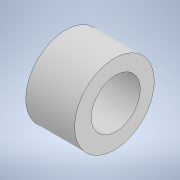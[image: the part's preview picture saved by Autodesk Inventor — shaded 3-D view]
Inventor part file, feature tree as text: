
AUTODESK INVENTOR PART (.ipt)
format: ipt  version: 2021 (Build 250183000, 183)  size: 99,328 bytes
history: native  units: mm
features: extrude x1, sketch x1
ambient origin geometry x8: Origin, YZ Plane, XZ Plane, XY Plane, X Axis, Y Axis, Z Axis, Center Point
bodies: Solid1 (feature_tree)
feature tree (2):
  extrude  "Extrusion1"  Depth=16.0mm
  sketch  "Sketch1"  dims[d0=26.0mm d1=16.0mm d2=16.0mm d3=0.0mm]
